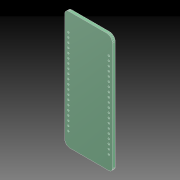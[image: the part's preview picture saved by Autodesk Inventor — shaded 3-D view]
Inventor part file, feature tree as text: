
AUTODESK INVENTOR PART (.ipt)
format: ipt  version: 2020 (Build 240168000, 168)  size: 242,176 bytes
history: native  units: mm
features: extrude x2, sketch x2, other x1
ambient origin geometry x8: Origin, YZ Plane, XZ Plane, XY Plane, X Axis, Y Axis, Z Axis, Center Point
bodies: Body1 (feature_tree)
feature tree (5):
  other  "Твердое тело1"
  extrude  "untitled.brdКонтур"  Depth=1.6mm TaperAngle=0.0deg
  extrude  "Выдавливание2"  Depth=30.75mm TaperAngle=0.0deg
  sketch  "Эскиз1"
  sketch  "Эскиз2"
